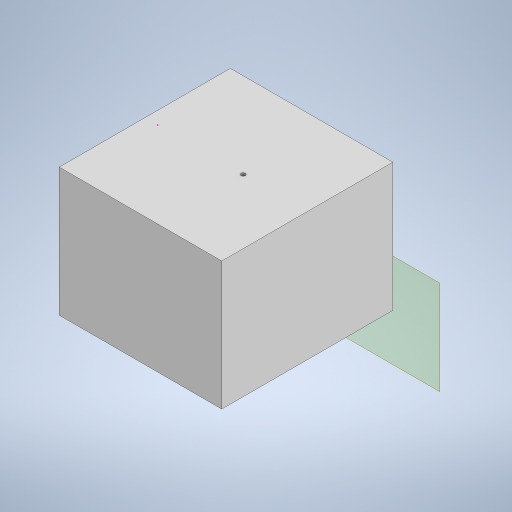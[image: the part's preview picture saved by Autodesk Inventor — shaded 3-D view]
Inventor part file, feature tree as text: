
AUTODESK INVENTOR PART (.ipt)
format: ipt  version: 2023 (Build 270158000, 158)  size: 286,208 bytes
history: native  units: mm
features: sketch x7, plane x6, extrude x5
ambient origin geometry x8: Origin, YZ Plane, XZ Plane, XY Plane, X Axis, Y Axis, Z Axis, Center Point
bodies: Body1 (feature_tree)
feature tree (18):
  plane  "Work Plane13"
  extrude  "Extrusion34"  Depth=40.0mm
  sketch  "Sketch46"  dims[d144=30.0mm d145=0.0mm d146=36.0mm]
  plane  "Work Plane11"
  extrude  "Extrusion35"  Depth=36.0mm
  sketch  "Sketch48"  dims[d150=0.0mm d151=0.0mm d156=20.0mm]
  extrude  "Extrusion36"  Depth=1.0mm
  plane  "Work Plane7"
  extrude  "Extrusion38"  Depth=20.0mm
  plane  "Work Plane4"
  extrude  "Extrusion39"  Depth=15.0mm TaperAngle=0.0deg
  plane  "Work Plane1"
  plane  "Work Plane6"
  sketch  "Sketch45"  dims[d142=38.0mm d143=40.0mm]
  sketch  "Sketch47"  dims[d147=30.0mm d148=-2.617994mm d149=1.0mm]
  sketch  "Sketch49"  dims[d157=15.0mm d158=15.0mm d159=0.0mm]
  sketch  "Sketch58"  dims[d160=3.0mm]
  sketch  "Sketch59"  dims[d161=20.0mm d162=35.0mm d163=0.0mm d49=0.5mm d50=0.872665mm d51=0.5mm d52=0.872665mm d130=0.5mm d131=0.872665mm d132=0.5mm d133=0.872665mm]
